# Revit family: Toilet_Paper_Holder-Double-Grohe-Essentials-41078_Series
name_source: partatom
category: Specialty Equipment
units: mm (PartAtom-declared; Revit-internal decimal feet)

## family parameters
Cut with Voids When Loaded = No
Host = Face
OmniClass Number = 23.40.20.21
OmniClass Title = Toilet and Bath Specialties
Part Type = Normal
Room Calculation Point = No
Round Connector Dimension = Use Diameter
Shared = Yes

## types (5) — shared parameters
Assembly Code = C1030200
Default Elevation = 0"
Description = Essentials Double Toilet Paper Holder
Disc Diameter = 2 1/8"
Height = 12 3/16"
Installation Type = Wall Mounted
Length = 4 9/16"
Manufacturer = Grohe
Product Page URL = https://www.grohe.us
URL = https://www.grohe.us

## per-type parameters (varying)
| type | Finish | Material |
| 410782431 | Metal-Grohe-2431-Matte Black | Metal-Grohe-2431-Matte Black |
| 41078000 | Metal-Grohe-000-StarLight Chrome | Metal-Grohe-000-StarLight Chrome |
| 41078A00 | Brass-Grohe-A00-Hard Graphite | Brass-Grohe-A00-Hard Graphite |
| 41078EN0 | Metal-Grohe-EN0-Brushed Nickel Infinity Finish | Metal-Grohe-EN0-Brushed Nickel Infinity Finish |
| 41078GN0 | Metal-Grohe-GN0-Brushed Cool Sunrise | Metal-Grohe-GN0-Brushed Cool Sunrise |

note: column(s) folded — value = type name in every type: Model

## geometry (parser evidence)
native form markers: Sweep x3
no freeform markers — native parametric forms only
